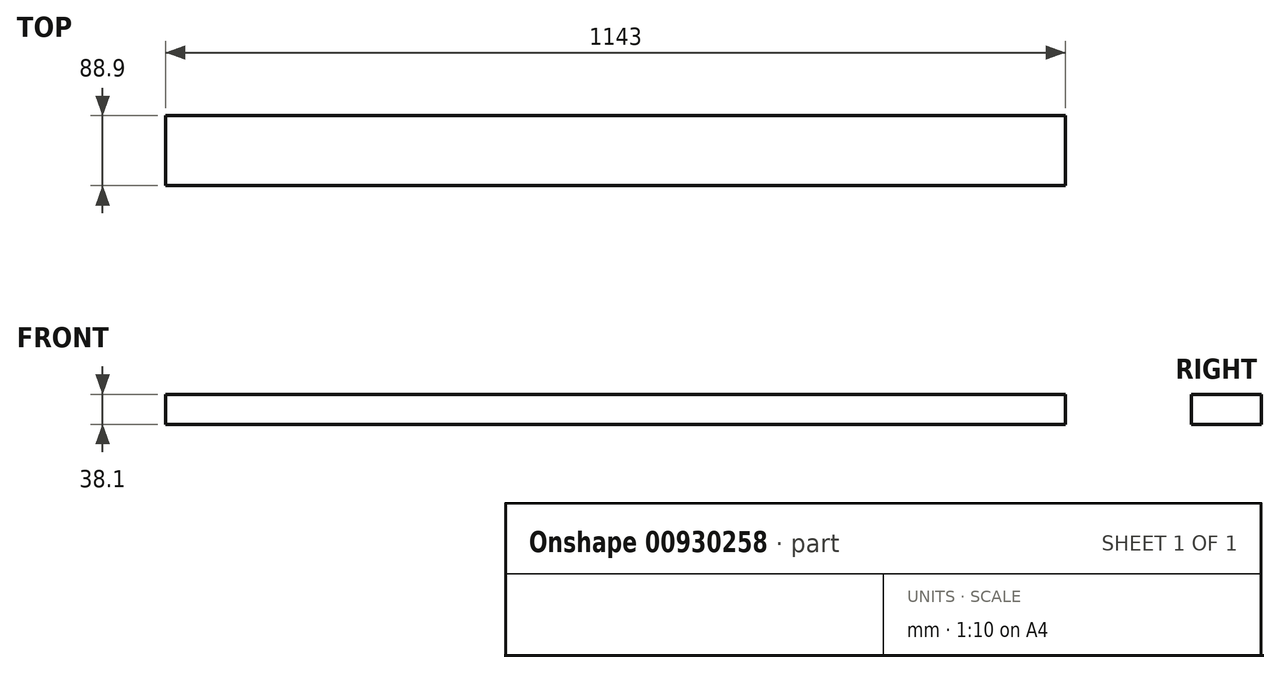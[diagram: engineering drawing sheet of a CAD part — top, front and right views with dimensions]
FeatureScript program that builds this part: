
annotation { "Feature Type Name" : "Feature", "Feature Type Description" : "" }
export const myFeature = defineFeature(function(context is Context, id is Id, definition is map)
    precondition{}
    {
        {
            var Q0;
            Q0=qCreatedBy(makeId("Right.planeOp"),FACE);
            var sketch = newSketch(context, id + "F0", { "sketchPlane" : qUnion([Q0])});
            skLineSegment(sketch, "E0.bottom", {"start": v(44.45, -19.05) * mm, "end": v(-44.45, -19.05) * mm});
            skLineSegment(sketch, "E0.top", {"start": v(44.45, 19.05) * mm, "end": v(-44.45, 19.05) * mm});
            skLineSegment(sketch, "E0.left", {"start": v(44.45, -19.05) * mm, "end": v(44.45, 19.05) * mm});
            skLineSegment(sketch, "E0.right", {"start": v(-44.45, -19.05) * mm, "end": v(-44.45, 19.05) * mm});
            skPoint(sketch, "E0.middle", {"position": v(0, 0) * mm});
            skSolve(sketch);
        }
        {
            var Q0;
            Q0=qSketchRegion(id+"F0",true);
            extrude(context, id + "F1", {"entities" : qUnion([Q0]), "endBound" : BoundingType.SYMMETRIC, "depth" : 1143 * mm});
        }
    });
